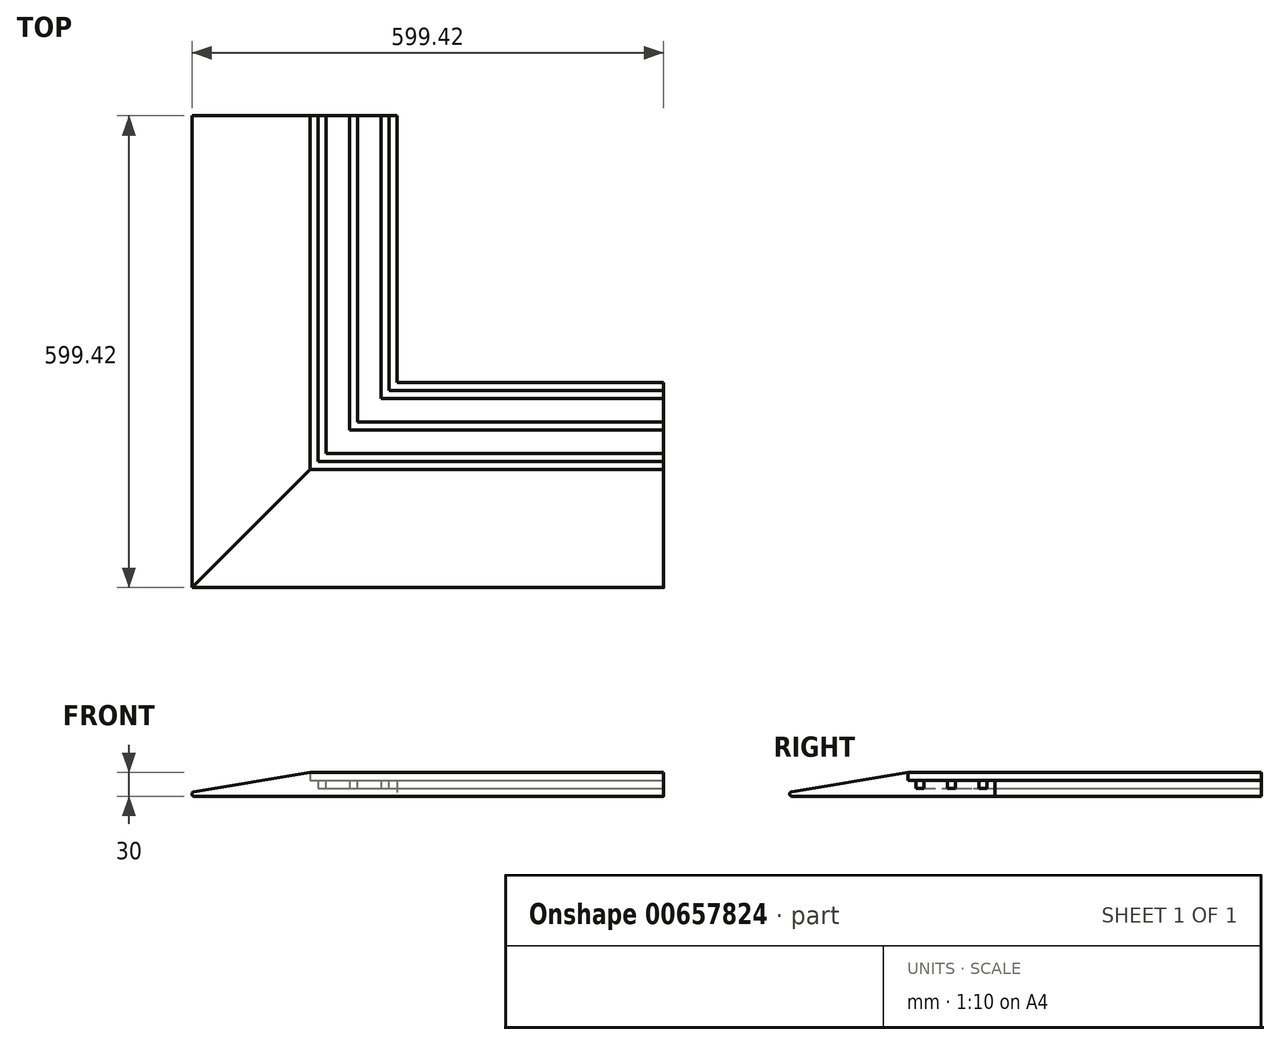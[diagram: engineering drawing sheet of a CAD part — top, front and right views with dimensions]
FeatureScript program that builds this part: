
annotation { "Feature Type Name" : "Feature", "Feature Type Description" : "" }
export const myFeature = defineFeature(function(context is Context, id is Id, definition is map)
    precondition{}
    {
        {
            var Q0;
            Q0=qCreatedBy(makeId("Front.planeOp"),FACE);
            var sketch = newSketch(context, id + "F0", { "sketchPlane" : qUnion([Q0])});
            skLineSegment(sketch, "E0.bottom", {"start": v(0, 0) * mm, "end": v(-150, 0) * mm});
            skLineSegment(sketch, "E0.top", {"start": v(0, -30) * mm, "end": v(-150, -30) * mm});
            skLineSegment(sketch, "E0.left", {"start": v(0, 0) * mm, "end": v(0, -30) * mm});
            skLineSegment(sketch, "E0.right", {"start": v(-150, 0) * mm, "end": v(-150, -30) * mm});
            skLineSegment(sketch, "E1.bottom", {"start": v(0, -30) * mm, "end": v(100.42, -30) * mm});
            skLineSegment(sketch, "E1.top", {"start": v(0, -20) * mm, "end": v(100.42, -20) * mm});
            skLineSegment(sketch, "E1.left", {"start": v(0, -30) * mm, "end": v(0, -20) * mm});
            skLineSegment(sketch, "E1.right", {"start": v(100.42, -30) * mm, "end": v(100.42, -20) * mm});
            skLineSegment(sketch, "E2.bottom", {"start": v(0, -20) * mm, "end": v(10.33, -20) * mm});
            skLineSegment(sketch, "E2.top", {"start": v(0, -10) * mm, "end": v(10.33, -10) * mm});
            skLineSegment(sketch, "E2.left", {"start": v(0, -20) * mm, "end": v(0, -10) * mm});
            skLineSegment(sketch, "E2.right", {"start": v(10.33, -20) * mm, "end": v(10.33, -10) * mm});
            skLineSegment(sketch, "E3", {"start": v(10.33, -20) * mm, "end": v(20.33, -20) * mm});
            skLineSegment(sketch, "E4.bottom", {"start": v(20.33, -20) * mm, "end": v(50.33, -20) * mm});
            skLineSegment(sketch, "E4.top", {"start": v(20.33, -10) * mm, "end": v(50.33, -10) * mm});
            skLineSegment(sketch, "E4.left", {"start": v(20.33, -20) * mm, "end": v(20.33, -10) * mm});
            skLineSegment(sketch, "E4.right", {"start": v(50.33, -20) * mm, "end": v(50.33, -10) * mm});
            skLineSegment(sketch, "E5", {"start": v(50.33, -20) * mm, "end": v(60.33, -20) * mm});
            skLineSegment(sketch, "E6.bottom", {"start": v(60.33, -20) * mm, "end": v(90.33, -20) * mm});
            skLineSegment(sketch, "E6.top", {"start": v(60.33, -10) * mm, "end": v(90.33, -10) * mm});
            skLineSegment(sketch, "E6.left", {"start": v(60.33, -20) * mm, "end": v(60.33, -10) * mm});
            skLineSegment(sketch, "E6.right", {"start": v(90.33, -20) * mm, "end": v(90.33, -10) * mm});
            skLineSegment(sketch, "E7.bottom", {"start": v(100.42, -30) * mm, "end": v(110.42, -30) * mm});
            skLineSegment(sketch, "E7.top", {"start": v(100.42, -10) * mm, "end": v(110.42, -10) * mm});
            skLineSegment(sketch, "E7.left", {"start": v(100.42, -30) * mm, "end": v(100.42, -10) * mm});
            skLineSegment(sketch, "E7.right", {"start": v(110.42, -30) * mm, "end": v(110.42, -10) * mm});
            skSolve(sketch);
        }
        {
            var Q0;
            {var subQ1=sQuery(id+"F0.wireOp",EDGE,"E1.right");var subQ2=makeQuery(id+"F0.imprint","IMPRINT",EDGE,{"derivedFrom":subQ1});var subQ9=sQuery(id+"F0.wireOp",EDGE,"E1.bottom");var subQ22=sQuery(id+"F0.wireOp",EDGE,"E2.top");var subQ25=sQuery(id+"F0.wireOp",EDGE,"E0.bottom");Q0=qUnion([makeQuery(id+"F0.imprint","IMPRINT",FACE,{"disambiguationData":[TD([[makeQuery(id+"F0.imprint","IMPRINT",EDGE,{"derivedFrom":subQ25}),1.0]])]}),makeQuery(id+"F0.imprint","IMPRINT",FACE,{"disambiguationData":[TD([[makeQuery(id+"F0.imprint","IMPRINT",EDGE,{"derivedFrom":sQuery(id+"F0.wireOp",EDGE,"E6.top")}),-1.0]])]}),makeQuery(id+"F0.imprint","IMPRINT",FACE,{"disambiguationData":[TD([[makeQuery(id+"F0.imprint","IMPRINT",EDGE,{"derivedFrom":subQ22}),-1.0]])]}),makeQuery(id+"F0.imprint","IMPRINT",FACE,{"disambiguationData":[TD([[makeQuery(id+"F0.imprint","IMPRINT",EDGE,{"derivedFrom":sQuery(id+"F0.wireOp",EDGE,"E4.top")}),-1.0]])]}),makeQuery(id+"F0.imprint","IMPRINT",FACE,{"disambiguationData":[TD([[makeQuery(id+"F0.imprint","IMPRINT",EDGE,{"derivedFrom":subQ9}),1.0]])]}),makeQuery(id+"F0.imprint","IMPRINT",FACE,{"disambiguationData":[TD([[subQ2,-1.0]])]})]);}
            extrude(context, id + "F1", {"entities" : qUnion([Q0]), "depth" : 600 * mm, "offsetDistance" : 25 * mm});
        }
        {
            var Q0;
            Q0=makeQuery(id+"F1.opExtrude","CAP_EDGE",EDGE,{"disambiguationData":[OSD([sQuery(id+"F0.wireOp",EDGE,"E7.right")])],"isStart":false});
            chamfer(context, id + "F2", {"entities" : qUnion([Q0]), "width" : 261 * mm, "tangentPropagation" : true});
        }
        {
            var Q0;
            Q0=makeQuery(id+"F1.opExtrude","SWEPT_EDGE",EDGE,{"disambiguationData":[OSD([sQuery(id+"F0.wireOp",EDGE,"E0.bottom"),sQuery(id+"F0.wireOp",EDGE,"E0.right")])]});
            chamfer(context, id + "F3", {"entities" : qUnion([Q0]), "chamferType" : ChamferType.TWO_OFFSETS, "width1" : 25 * mm, "oppositeDirection" : false, "width2" : 150 * mm, "tangentPropagation" : true});
        }
        {
            var Q0;
            {var subQ0=sQuery(id+"F0.wireOp",EDGE,"E0.right");Q0=makeQuery(id+"F3.opChamfer","BLEND_EDGE",EDGE,{"blendedFrom":[makeQuery(id+"F1.opExtrude","SWEPT_EDGE",EDGE,{"disambiguationData":[OSD([sQuery(id+"F0.wireOp",EDGE,"E0.bottom"),subQ0])]}),makeQuery(id+"F1.opExtrude","SWEPT_FACE",FACE,{"disambiguationData":[OSD([subQ0])]})],"blendedInto":[makeQuery(id+"F1.opExtrude","SWEPT_FACE",FACE,{"disambiguationData":[OSD([subQ0])]})]});}
            var Q1;
            Q1=makeQuery(id+"F1.opExtrude","SWEPT_EDGE",EDGE,{"disambiguationData":[OSD([sQuery(id+"F0.wireOp",EDGE,"E0.top"),sQuery(id+"F0.wireOp",EDGE,"E0.right")])]});
            fillet(context, id + "F4", {"entities" : qUnion([Q0, Q1]), "radius" : 2.5 * mm, "tangentPropagation" : true, "allowEdgeOverflow" : false});
        }
        {
            var Q0;
            Q0=makeQuery(id+"F1.opExtrude","SWEPT_BODY",BODY,{"disambiguationData":[OSD([sQuery(id+"F0.wireOp",EDGE,"E0.bottom"),sQuery(id+"F0.wireOp",EDGE,"E0.top"),sQuery(id+"F0.wireOp",EDGE,"E0.left"),sQuery(id+"F0.wireOp",EDGE,"E0.right"),sQuery(id+"F0.wireOp",EDGE,"E1.bottom"),sQuery(id+"F0.wireOp",EDGE,"E1.top"),sQuery(id+"F0.wireOp",EDGE,"E2.top"),sQuery(id+"F0.wireOp",EDGE,"E2.right"),sQuery(id+"F0.wireOp",EDGE,"E4.top"),sQuery(id+"F0.wireOp",EDGE,"E4.left"),sQuery(id+"F0.wireOp",EDGE,"E4.right"),sQuery(id+"F0.wireOp",EDGE,"E6.top"),sQuery(id+"F0.wireOp",EDGE,"E6.left"),sQuery(id+"F0.wireOp",EDGE,"E6.right"),sQuery(id+"F0.wireOp",EDGE,"E7.bottom"),sQuery(id+"F0.wireOp",EDGE,"E7.top"),sQuery(id+"F0.wireOp",EDGE,"E7.left"),sQuery(id+"F0.wireOp",EDGE,"E7.right")])]});
            var Q1;
            Q1=makeQuery(id+"F2.opChamfer","BLEND_FACE",FACE,{"disambiguationData":[OSD([sQuery(id+"F0.wireOp",EDGE,"E7.right")])]});
            mirror(context, id + "F5", {"operationType" : NewBodyOperationType.ADD, "entities" : qUnion([Q0]), "mirrorPlane" : qUnion([Q1])});
        }
    });
